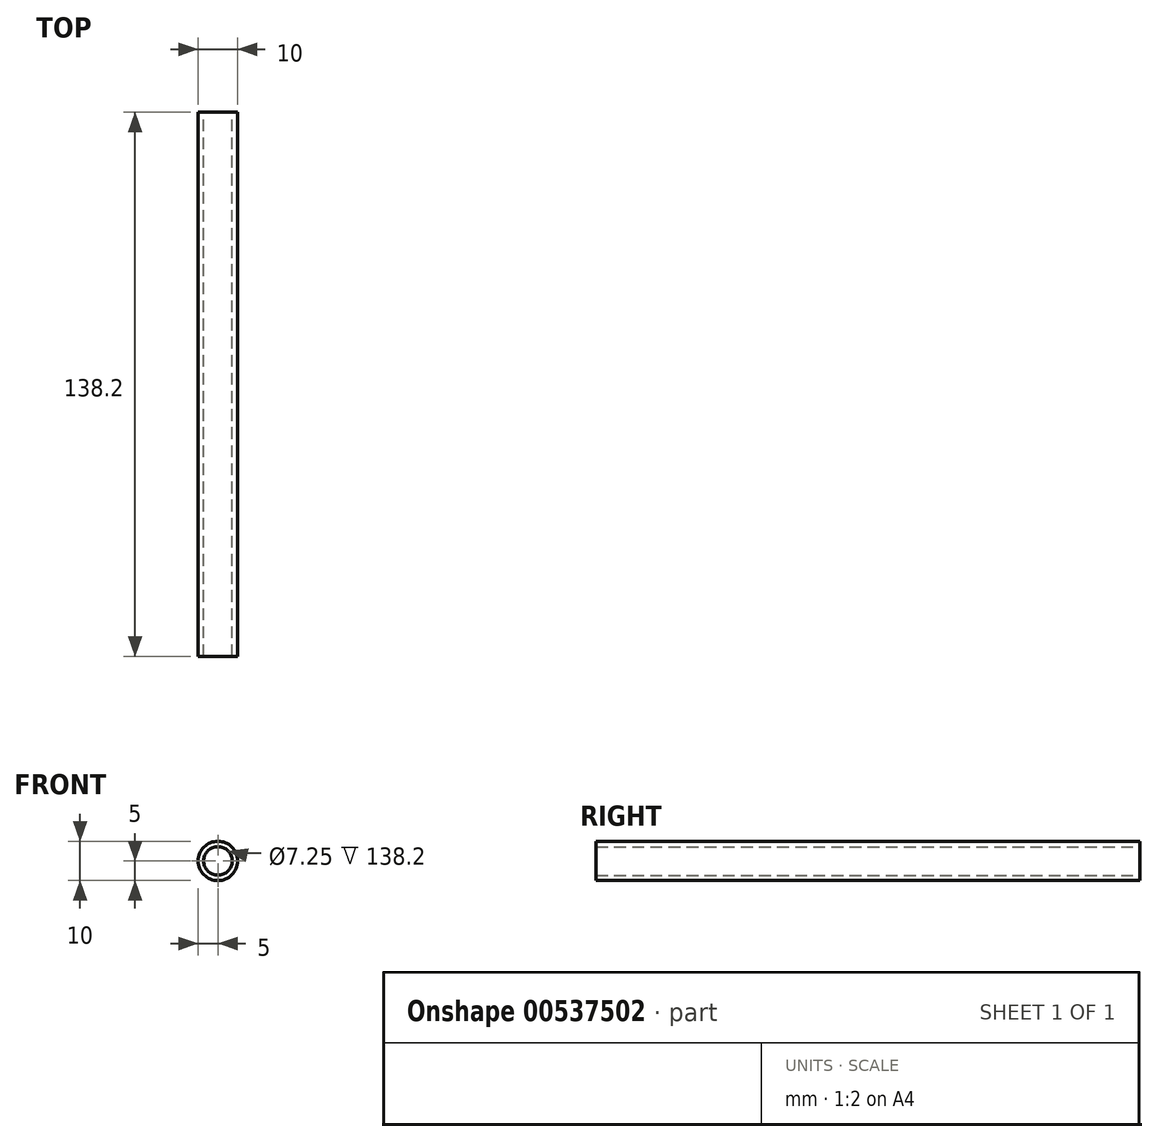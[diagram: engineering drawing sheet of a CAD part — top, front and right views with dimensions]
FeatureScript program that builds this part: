
annotation { "Feature Type Name" : "Feature", "Feature Type Description" : "" }
export const myFeature = defineFeature(function(context is Context, id is Id, definition is map)
    precondition{}
    {
        {
            var Q0;
            Q0=qCreatedBy(makeId("Front.planeOp"),FACE);
            var sketch = newSketch(context, id + "F0", { "sketchPlane" : qUnion([Q0])});
            skCircle(sketch, "E0", {"center": v(0, 0) * mm, "radius": 5 * mm});
            skCircle(sketch, "E1", {"center": v(0, 0) * mm, "radius": 3.63 * mm});
            skSolve(sketch);
        }
        {
            var Q0;
            Q0 = qSketchRegion(id + "F0", true);
            extrude(context, id + "F1", {"entities" : qUnion([Q0]), "endBound" : BoundingType.SYMMETRIC, "depth" : 138.2 * mm, "offsetDistance" : 25 * mm});
        }
    });
